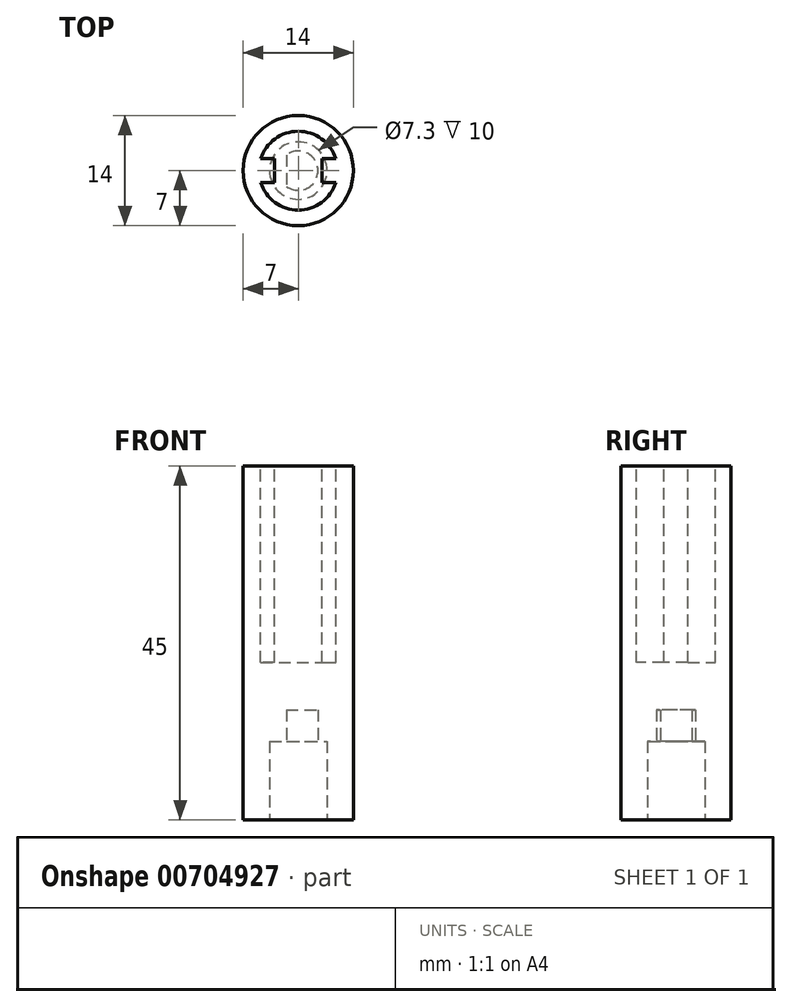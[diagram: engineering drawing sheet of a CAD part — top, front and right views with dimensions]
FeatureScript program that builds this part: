
annotation { "Feature Type Name" : "Feature", "Feature Type Description" : "" }
export const myFeature = defineFeature(function(context is Context, id is Id, definition is map)
    precondition{}
    {
        {
            var Q0;
            Q0=qCreatedBy(makeId("Top.planeOp"),FACE);
            var sketch = newSketch(context, id + "F0", { "sketchPlane" : qUnion([Q0])});
            skCircle(sketch, "E0", {"center": v(0, 0) * mm, "radius": 7 * mm});
            skSolve(sketch);
        }
        {
            var Q0;
            Q0 = qSketchRegion(id + "F0", true);
            extrude(context, id + "F1", {"entities" : qUnion([Q0]), "depth" : 45 * mm, "offsetDistance" : 25 * mm});
        }
        {
            var Q0;
            Q0=makeQuery(id+"F1.opExtrude","CAP_FACE",FACE,{"disambiguationData":[OSD([sQuery(id+"F0.wireOp",EDGE,"E0")])],"isStart":false});
            var sketch = newSketch(context, id + "F2", { "sketchPlane" : qUnion([Q0])});
            skLineSegment(sketch, "E1", {"start": v(-12.72, 0) * mm, "end": v(15, 0) * mm, "construction": true});
            skLineSegment(sketch, "E2", {"start": v(0, 9.15) * mm, "end": v(0, -8.81) * mm, "construction": true});
            skLineSegment(sketch, "E3", {"start": v(-4.77, 1.5) * mm, "end": v(-3, 1.5) * mm});
            skLineSegment(sketch, "E4", {"start": v(-3, 1.5) * mm, "end": v(-3, -1.5) * mm});
            skLineSegment(sketch, "E5", {"start": v(-3, -1.5) * mm, "end": v(-4.77, -1.5) * mm});
            skLineSegment(sketch, "E6", {"start": v(4.77, 1.5) * mm, "end": v(3, 1.5) * mm});
            skLineSegment(sketch, "E7", {"start": v(3, 1.5) * mm, "end": v(3, -1.5) * mm});
            skLineSegment(sketch, "E8", {"start": v(3, -1.5) * mm, "end": v(4.77, -1.5) * mm});
            skArc(sketch, "E9", {"start": v(-4.77, -1.5) * mm, "mid": v(0, -5) * mm, "end": v(4.77, -1.5) * mm});
            skArc(sketch, "E10", {"start": v(4.77, 1.5) * mm, "mid": v(0, 5) * mm, "end": v(-4.77, 1.5) * mm});
            skSolve(sketch);
        }
        {
            var Q0;
            Q0=makeQuery(id+"F2.imprint","IMPRINT",FACE,{"disambiguationData":[TD([[makeQuery(id+"F2.imprint","IMPRINT",EDGE,{"derivedFrom":sQuery(id+"F2.wireOp",EDGE,"E3")}),1.0]])]});
            extrude(context, id + "F3", {"entities" : qUnion([Q0]), "operationType" : NewBodyOperationType.REMOVE, "oppositeDirection" : true, "depth" : 25 * mm, "offsetDistance" : 25 * mm});
        }
        {
            var Q0;
            Q0=makeQuery(id+"F1.opExtrude","CAP_FACE",FACE,{"disambiguationData":[OSD([sQuery(id+"F0.wireOp",EDGE,"E0")])],"isStart":true});
            var sketch = newSketch(context, id + "F4", { "sketchPlane" : qUnion([Q0])});
            skCircle(sketch, "E11", {"center": v(0, 0) * mm, "radius": 3.65 * mm});
            skSolve(sketch);
        }
        {
            var Q0;
            Q0=makeQuery(id+"F4.imprint","IMPRINT",FACE,{"disambiguationData":[TD([[makeQuery(id+"F4.imprint","IMPRINT",EDGE,{"derivedFrom":sQuery(id+"F4.wireOp",EDGE,"E11")}),1.0]])]});
            extrude(context, id + "F5", {"entities" : qUnion([Q0]), "operationType" : NewBodyOperationType.REMOVE, "oppositeDirection" : true, "depth" : 10 * mm, "offsetDistance" : 25 * mm});
        }
        {
            var Q0;
            Q0=makeQuery(id+"F5.boolean.opBoolean","COPY",FACE,{"derivedFrom":makeQuery(id+"F5.opExtrude","CAP_FACE",FACE,{"disambiguationData":[OSD([sQuery(id+"F4.wireOp",EDGE,"E11")])],"isStart":false})});
            var sketch = newSketch(context, id + "F6", { "sketchPlane" : qUnion([Q0])});
            skLineSegment(sketch, "E12", {"start": v(-1.5, -2) * mm, "end": v(-1.5, 2) * mm});
            skArc(sketch, "E13", {"start": v(-1.5, -2) * mm, "mid": v(2.5, 0) * mm, "end": v(-1.5, 2) * mm});
            skSolve(sketch);
        }
        {
            var Q0;
            Q0=makeQuery(id+"F6.imprint","IMPRINT",FACE,{"disambiguationData":[TD([[makeQuery(id+"F6.imprint","IMPRINT",EDGE,{"derivedFrom":sQuery(id+"F6.wireOp",EDGE,"E12")}),-1.0]])]});
            extrude(context, id + "F7", {"entities" : qUnion([Q0]), "operationType" : NewBodyOperationType.REMOVE, "oppositeDirection" : true, "depth" : 4 * mm, "offsetDistance" : 25 * mm});
        }
    });
